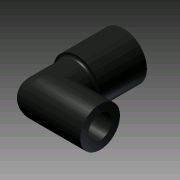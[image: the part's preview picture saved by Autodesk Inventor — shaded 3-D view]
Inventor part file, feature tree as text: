
AUTODESK INVENTOR PART (.ipt)
format: ipt  version: 2011 (Build 150239000, 239)  size: 158,208 bytes
history: native  units: in
note: dims shown in document units (in); Inventor stores cm internally (conversion verified against a paired STEP export)
features: extrude x5, sketch x4, plane x2, fillet x2, projected_geometry x1
ambient origin geometry x8: Origin, YZ Plane, XZ Plane, XY Plane, X Axis, Y Axis, Z Axis, Center Point
bodies: Solid1 (feature_tree)
feature tree (14):
  extrude  "Extrusion1"  Depth=0.5in
  extrude  "Extrusion2"  Depth=0.425in
  plane  "Work Plane1"
  sketch  "Sketch3"  dims[d5=0.5in d6=0.0in d7=-0.83in]
  extrude  "Extrusion3"  [1 undecoded]
  extrude  "Extrusion4"  Depth=0.25in
  plane  "Work Plane2"
  extrude  "Extrusion5"  Depth=0.75in TaperAngle=0.0deg
  fillet  "Fillet1"  Radius=1.0in
  fillet  "Fillet2"  Radius=0.5in
  sketch  "Sketch1"  dims[d0=0.25in d1=0.5in]
  sketch  "Sketch2"  dims[d2=0.5in d3=0.0in d4=0.425in]
  projected_geometry  "Projected Loop1"
  sketch  "Sketch4"  dims[d8=0.75in d9=0.0in d10=0.25in d11=0.75in d12=0.0in d13=1.0in d14=0.5in d15=0.0in d16=0.125in d17=0.025in]
note: 1 required parameter value undecoded (feature->parameter linkage not recoverable at this tier; creation-order binding heuristic only, values carry confidence <= 0.55)
